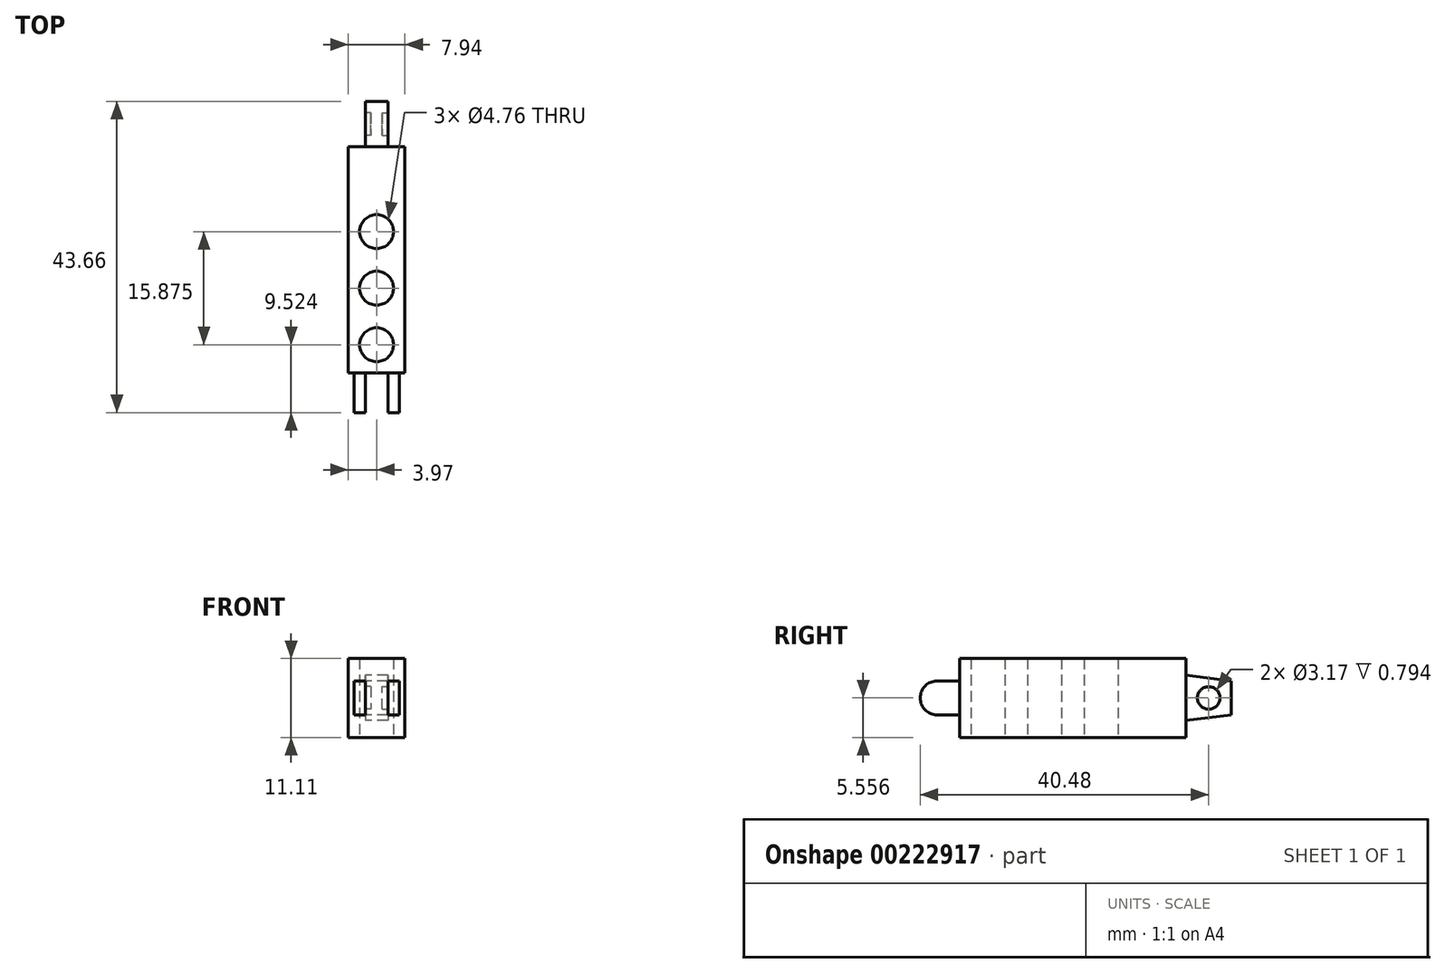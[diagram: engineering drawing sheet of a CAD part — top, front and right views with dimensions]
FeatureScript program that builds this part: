
annotation { "Feature Type Name" : "Feature", "Feature Type Description" : "" }
export const myFeature = defineFeature(function(context is Context, id is Id, definition is map)
    precondition{}
    {
        {
            var Q0;
            Q0=qCreatedBy(makeId("Top.planeOp"),FACE);
            var sketch = newSketch(context, id + "F0", { "sketchPlane" : qUnion([Q0])});
            skLineSegment(sketch, "E0.bottom", {"start": v(-3.97, 15.88) * mm, "end": v(3.97, 15.88) * mm});
            skLineSegment(sketch, "E0.top", {"start": v(-3.97, -15.88) * mm, "end": v(3.97, -15.88) * mm});
            skLineSegment(sketch, "E0.left", {"start": v(-3.97, 15.88) * mm, "end": v(-3.97, -15.88) * mm});
            skLineSegment(sketch, "E0.right", {"start": v(3.97, 15.88) * mm, "end": v(3.97, -15.88) * mm});
            skPoint(sketch, "E0.middle", {"position": v(0, 0) * mm});
            skCircle(sketch, "E1", {"center": v(0, 11.9) * mm, "radius": 2.38 * mm});
            skCircle(sketch, "E2.MirrorC", {"center": v(0, -11.9) * mm, "radius": 2.38 * mm});
            skCircle(sketch, "E3.0.1.0", {"center": v(0, -3.97) * mm, "radius": 2.38 * mm});
            skCircle(sketch, "E3.0.2.0", {"center": v(0, 3.97) * mm, "radius": 2.38 * mm});
            skLineSegment(sketch, "E3.direction2", {"start": v(0, -11.9) * mm, "end": v(0, -3.97) * mm, "construction": true});
            skSolve(sketch);
        }
        {
            var Q0;
            Q0=qSketchRegion(id+"F0",true);
            extrude(context, id + "F1", {"entities" : qUnion([Q0]), "depth" : 9.52 * mm});
        }
        {
            var Q0;
            Q0=makeQuery(id+"F0.imprint","IMPRINT",FACE,{"disambiguationData":[TD([[makeQuery(id+"F0.imprint","IMPRINT",EDGE,{"derivedFrom":sQuery(id+"F0.wireOp",EDGE,"E1")}),1.0]])]});
            var Q1;
            Q1=makeQuery(id+"F0.imprint","IMPRINT",FACE,{"disambiguationData":[TD([[makeQuery(id+"F0.imprint","IMPRINT",EDGE,{"derivedFrom":sQuery(id+"F0.wireOp",EDGE,"E2.MirrorC")}),-1.0]])]});
            var Q2;
            Q2=makeQuery(id+"F0.imprint","IMPRINT",FACE,{"disambiguationData":[TD([[makeQuery(id+"F0.imprint","IMPRINT",EDGE,{"derivedFrom":sQuery(id+"F0.wireOp",EDGE,"E3.0.2.0")}),-1.0]])]});
            var Q3;
            Q3=makeQuery(id+"F0.imprint","IMPRINT",FACE,{"disambiguationData":[TD([[makeQuery(id+"F0.imprint","IMPRINT",EDGE,{"derivedFrom":sQuery(id+"F0.wireOp",EDGE,"E3.0.1.0")}),-1.0]])]});
            extrude(context, id + "F2", {"entities" : qUnion([Q0, Q1, Q2, Q3]), "operationType" : NewBodyOperationType.ADD, "depth" : 11.1 * mm});
        }
        {
            var Q0;
            Q0=qCreatedBy(makeId("Right.planeOp"),FACE);
            var sketch = newSketch(context, id + "F3", { "sketchPlane" : qUnion([Q0])});
            skLineSegment(sketch, "E4", {"start": v(0, 5.56) * mm, "end": v(-15.88, 5.56) * mm});
            skLineSegment(sketch, "E5", {"start": v(-15.88, 5.56) * mm, "end": v(-15.88, 7.94) * mm});
            skLineSegment(sketch, "E6.bottom", {"start": v(-15.88, 7.94) * mm, "end": v(-19.05, 7.94) * mm});
            skLineSegment(sketch, "E6.top", {"start": v(-15.88, 5.56) * mm, "end": v(-19.05, 5.56) * mm});
            skLineSegment(sketch, "E6.left", {"start": v(-15.88, 7.94) * mm, "end": v(-15.88, 5.56) * mm});
            skLineSegment(sketch, "E6.right", {"start": v(-19.05, 7.94) * mm, "end": v(-19.05, 5.56) * mm});
            skLineSegment(sketch, "E7.MirrorCS", {"start": v(-19.05, 3.17) * mm, "end": v(-19.05, 5.56) * mm});
            skLineSegment(sketch, "E8.MirrorCS", {"start": v(-15.88, 3.17) * mm, "end": v(-19.05, 3.17) * mm});
            skLineSegment(sketch, "E9.MirrorCS", {"start": v(-15.88, 3.17) * mm, "end": v(-15.88, 5.56) * mm});
            skLineSegment(sketch, "E10", {"start": v(-19.05, 5.56) * mm, "end": v(-21.43, 5.56) * mm});
            skArc(sketch, "E11", {"start": v(-19.05, 7.94) * mm, "mid": v(-21.43, 5.56) * mm, "end": v(-19.05, 3.17) * mm});
            skLineSegment(sketch, "E12", {"start": v(0, 5.56) * mm, "end": v(15.88, 5.56) * mm});
            skLineSegment(sketch, "E13", {"start": v(15.88, 5.56) * mm, "end": v(22.23, 5.56) * mm});
            skLineSegment(sketch, "E14", {"start": v(22.23, 5.56) * mm, "end": v(22.23, 7.94) * mm});
            skLineSegment(sketch, "E15", {"start": v(22.23, 7.94) * mm, "end": v(15.88, 8.73) * mm});
            skLineSegment(sketch, "E16", {"start": v(15.88, 8.73) * mm, "end": v(15.88, 5.56) * mm});
            skLineSegment(sketch, "E17.MirrorCS", {"start": v(22.23, 5.56) * mm, "end": v(22.23, 3.17) * mm});
            skLineSegment(sketch, "E18.MirrorCS", {"start": v(22.23, 3.17) * mm, "end": v(15.88, 2.38) * mm});
            skLineSegment(sketch, "E19.MirrorCS", {"start": v(15.88, 2.38) * mm, "end": v(15.88, 5.56) * mm});
            skLineSegment(sketch, "E20", {"start": v(0, 5.56) * mm, "end": v(0, 0) * mm});
            skSolve(sketch);
        }
        {
            var Q0;
            Q0=makeQuery(id+"F3.imprint","IMPRINT",FACE,{"disambiguationData":[TD([[makeQuery(id+"F3.imprint","IMPRINT",EDGE,{"derivedFrom":sQuery(id+"F3.wireOp",EDGE,"E6.bottom")}),1.0]])]});
            var Q1;
            Q1=makeQuery(id+"F3.imprint","IMPRINT",FACE,{"disambiguationData":[TD([[makeQuery(id+"F3.imprint","IMPRINT",EDGE,{"derivedFrom":sQuery(id+"F3.wireOp",EDGE,"E6.top")}),1.0]])]});
            var Q2;
            {var subQ0=sQuery(id+"F3.wireOp",EDGE,"E6.right");Q2=makeQuery(id+"F3.imprint","IMPRINT",FACE,{"disambiguationData":[TD([[makeQuery(id+"F3.imprint","IMPRINT",EDGE,{"derivedFrom":subQ0}),-1.0]])]});}
            var Q3;
            {var subQ0=sQuery(id+"F3.wireOp",EDGE,"E7.MirrorCS");Q3=makeQuery(id+"F3.imprint","IMPRINT",FACE,{"disambiguationData":[TD([[makeQuery(id+"F3.imprint","IMPRINT",EDGE,{"derivedFrom":subQ0}),1.0]])]});}
            extrude(context, id + "F4", {"entities" : qUnion([Q0, Q1, Q2, Q3]), "operationType" : NewBodyOperationType.ADD, "endBound" : BoundingType.SYMMETRIC, "depth" : 6.35 * mm});
        }
        {
            var Q0;
            Q0=makeQuery(id+"F4.opExtrude","SWEPT_FACE",FACE,{"disambiguationData":[OSD([sQuery(id+"F3.wireOp",EDGE,"E6.bottom")])]});
            var sketch = newSketch(context, id + "F5", { "sketchPlane" : qUnion([Q0])});
            skLineSegment(sketch, "E21", {"start": v(0, -15.88) * mm, "end": v(0, -22.23) * mm});
            skPoint(sketch, "E21.endSnap0", {"position": v(0, -19.05) * mm});
            skLineSegment(sketch, "E22", {"start": v(0, -22.23) * mm, "end": v(-1.59, -22.23) * mm});
            skLineSegment(sketch, "E23", {"start": v(-1.59, -22.23) * mm, "end": v(-1.59, -15.88) * mm});
            skLineSegment(sketch, "E24", {"start": v(-1.59, -15.88) * mm, "end": v(0, -15.88) * mm});
            skLineSegment(sketch, "E25.MirrorCS", {"start": v(1.59, -15.88) * mm, "end": v(0, -15.88) * mm});
            skLineSegment(sketch, "E26.MirrorCS", {"start": v(1.59, -22.23) * mm, "end": v(1.59, -15.88) * mm});
            skLineSegment(sketch, "E27.MirrorCS", {"start": v(0, -22.23) * mm, "end": v(1.59, -22.23) * mm});
            skSolve(sketch);
        }
        {
            var Q0;
            Q0=qSketchRegion(id+"F5",true);
            extrude(context, id + "F6", {"entities" : qUnion([Q0]), "operationType" : NewBodyOperationType.REMOVE, "oppositeDirection" : true, "depth" : 6.35 * mm});
        }
        {
            var Q0;
            Q0=makeQuery(id+"F3.imprint","IMPRINT",FACE,{"disambiguationData":[TD([[makeQuery(id+"F3.imprint","IMPRINT",EDGE,{"derivedFrom":sQuery(id+"F3.wireOp",EDGE,"E13")}),1.0]])]});
            var Q1;
            Q1=makeQuery(id+"F3.imprint","IMPRINT",FACE,{"disambiguationData":[TD([[makeQuery(id+"F3.imprint","IMPRINT",EDGE,{"derivedFrom":sQuery(id+"F3.wireOp",EDGE,"E13")}),-1.0]])]});
            extrude(context, id + "F7", {"entities" : qUnion([Q0, Q1]), "operationType" : NewBodyOperationType.ADD, "endBound" : BoundingType.SYMMETRIC, "depth" : 3.17 * mm});
        }
        {
            var Q0;
            Q0=makeQuery(id+"F7.opExtrude","CAP_FACE",FACE,{"disambiguationData":[OSD([sQuery(id+"F3.wireOp",EDGE,"E14"),sQuery(id+"F3.wireOp",EDGE,"E15"),sQuery(id+"F3.wireOp",EDGE,"E16"),sQuery(id+"F3.wireOp",EDGE,"E17.MirrorCS"),sQuery(id+"F3.wireOp",EDGE,"E18.MirrorCS"),sQuery(id+"F3.wireOp",EDGE,"E19.MirrorCS")])],"isStart":false});
            var sketch = newSketch(context, id + "F8", { "sketchPlane" : qUnion([Q0])});
            skCircle(sketch, "E28", {"center": v(19.05, 5.56) * mm, "radius": 1.59 * mm});
            skPoint(sketch, "E28.centerSnap0", {"position": v(22.23, 5.56) * mm});
            skSolve(sketch);
        }
        {
            var Q0;
            Q0=qSketchRegion(id+"F8",true);
            extrude(context, id + "F9", {"entities" : qUnion([Q0]), "operationType" : NewBodyOperationType.REMOVE, "oppositeDirection" : true, "depth" : 0.8 * mm});
        }
        {
            var Q0;
            Q0=makeQuery(id+"F7.opExtrude","CAP_FACE",FACE,{"disambiguationData":[OSD([sQuery(id+"F3.wireOp",EDGE,"E14"),sQuery(id+"F3.wireOp",EDGE,"E15"),sQuery(id+"F3.wireOp",EDGE,"E16"),sQuery(id+"F3.wireOp",EDGE,"E17.MirrorCS"),sQuery(id+"F3.wireOp",EDGE,"E18.MirrorCS"),sQuery(id+"F3.wireOp",EDGE,"E19.MirrorCS")])],"isStart":true});
            var sketch = newSketch(context, id + "F10", { "sketchPlane" : qUnion([Q0])});
            skCircle(sketch, "E29", {"center": v(-19.05, 5.56) * mm, "radius": 1.59 * mm});
            skSolve(sketch);
        }
        {
            var Q0;
            Q0=qSketchRegion(id+"F10",true);
            extrude(context, id + "F11", {"entities" : qUnion([Q0]), "operationType" : NewBodyOperationType.REMOVE, "oppositeDirection" : true, "depth" : 0.8 * mm});
        }
    });
